# Revit family: Ikea TRYSIL
name_source: partatom
category: Furniture
revit_build: Autodesk Revit 2016 (Build: 20150220_1215(x64)
units: mm (PartAtom-declared; Revit-internal decimal feet)

## family parameters
Always vertical = Yes
Cut with Voids When Loaded = No
OmniClass Number = 23.40.20.00
OmniClass Title = General Furniture and Specialties
Room Calculation Point = No
Shared = No
Work Plane-Based = No

## types (4) — shared parameters
Length = 2000 mm  [stored 6.56168 ft]
Mattrass Material = Linen, White

## per-type parameters (varying)
| type | Frame Material | Width | Wood Finish |
| 1600x2000 mm White | White Paint | 1600 mm  [stored 5.24934 ft] | White Paint |
| 1400x2000 mm white | White Paint | 1400 mm  [stored 4.59318 ft] | White Paint |
| 1600x2000 mm brown | Black luminium | 1600 mm  [stored 5.24934 ft] | Dark Wood Finish |
| 1400x2000 mm Brown | Black luminium | 1400 mm  [stored 4.59318 ft] | Dark Wood Finish |

note: [stored X ft] marks values corroborated as IEEE doubles in the binary element streams (Revit-internal decimal feet)

## geometry (parser evidence)
native form markers: Sweep x2
no freeform markers — native parametric forms only
